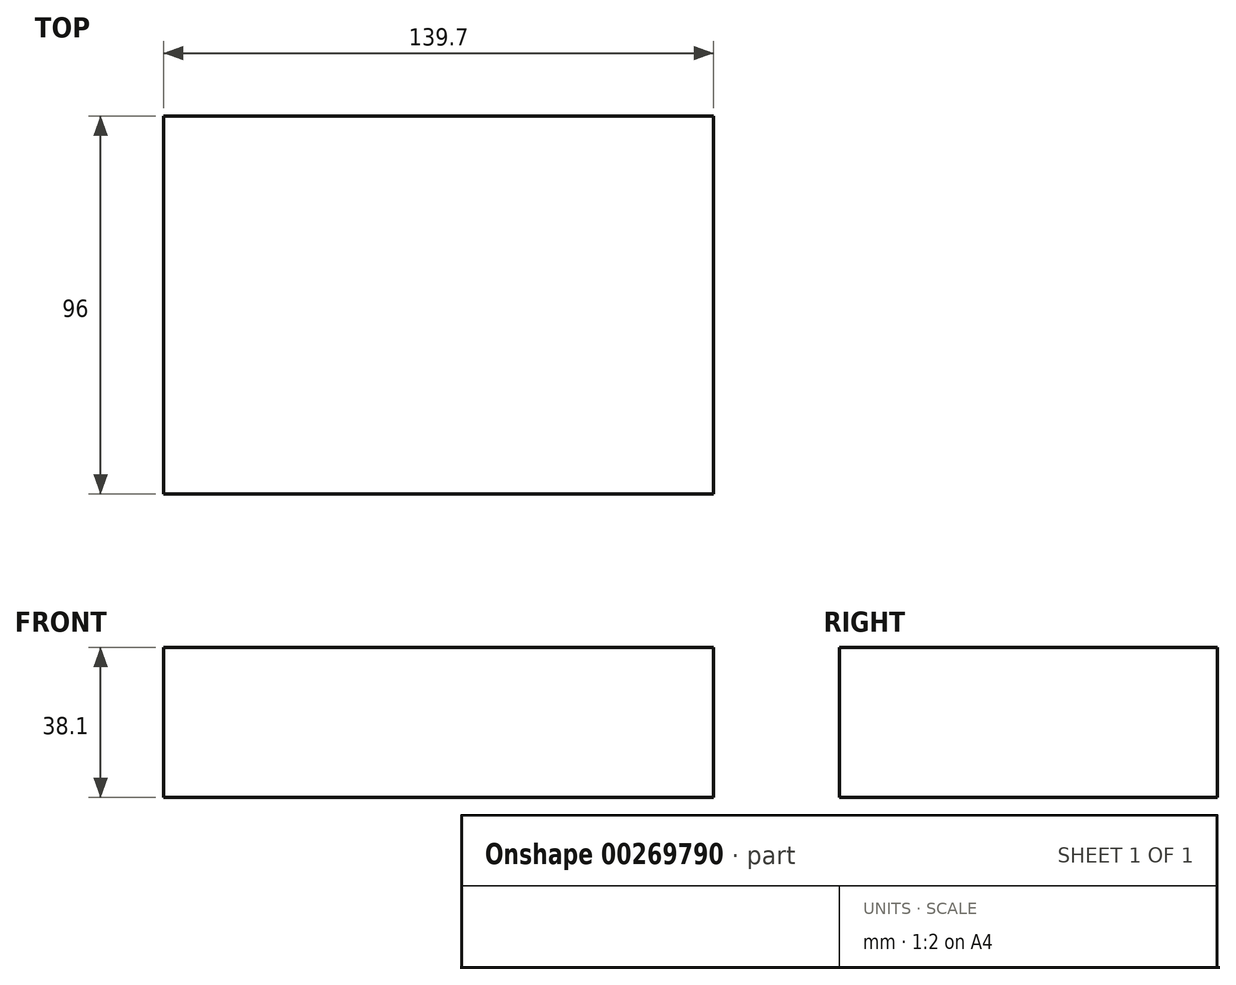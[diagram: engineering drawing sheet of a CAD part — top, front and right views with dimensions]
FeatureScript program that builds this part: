
annotation { "Feature Type Name" : "Feature", "Feature Type Description" : "" }
export const myFeature = defineFeature(function(context is Context, id is Id, definition is map)
    precondition{}
    {
        {
            var Q0;
            Q0=qCreatedBy(makeId("Front.planeOp"),FACE);
            var sketch = newSketch(context, id + "F0", { "sketchPlane" : qUnion([Q0])});
            skLineSegment(sketch, "E0", {"start": v(-361.95, 762) * mm, "end": v(361.95, 762) * mm, "construction": true});
            skPoint(sketch, "E1", {"position": v(0, 762) * mm});
            skLineSegment(sketch, "E2", {"start": v(-444.5, 457.2) * mm, "end": v(-730.25, 457.2) * mm});
            skLineSegment(sketch, "E3", {"start": v(444.5, 457.2) * mm, "end": v(730.25, 457.2) * mm});
            skLineSegment(sketch, "E4", {"start": v(-802.67, 255) * mm, "end": v(-903.42, 971.86) * mm});
            skLineSegment(sketch, "E5", {"start": v(-802.67, 255) * mm, "end": v(-361.95, 316.94) * mm, "construction": true});
            skLineSegment(sketch, "E6", {"start": v(-361.95, 762) * mm, "end": v(-361.95, 316.94) * mm, "construction": true});
            skLineSegment(sketch, "E7", {"start": v(95.25, 762) * mm, "end": v(95.25, 679.45) * mm, "construction": true});
            skLineSegment(sketch, "E8", {"start": v(-866.3, 707.76) * mm, "end": v(-784.56, 719.24) * mm, "construction": true});
            skLineSegment(sketch, "E9", {"start": v(95.25, 762) * mm, "end": v(361.95, 762) * mm, "construction": true});
            skLineSegment(sketch, "E10", {"start": v(-866.3, 707.76) * mm, "end": v(-903.42, 971.86) * mm, "construction": true});
            skLineSegment(sketch, "E11", {"start": v(-20.42, 164.2) * mm, "end": v(2.65, 0) * mm, "construction": true});
            skLineSegment(sketch, "E12", {"start": v(95.25, 679.45) * mm, "end": v(697.05, 0) * mm});
            skPoint(sketch, "E13", {"position": v(292.1, 457.2) * mm});
            skLineSegment(sketch, "E14.bottom", {"start": v(-361.95, 762) * mm, "end": v(-222.25, 762) * mm});
            skLineSegment(sketch, "E14.top", {"start": v(-361.95, 723.9) * mm, "end": v(-222.25, 723.9) * mm});
            skLineSegment(sketch, "E14.left", {"start": v(-361.95, 762) * mm, "end": v(-361.95, 723.9) * mm});
            skLineSegment(sketch, "E14.right", {"start": v(-222.25, 762) * mm, "end": v(-222.25, 723.9) * mm});
            skLineSegment(sketch, "E15.1.0.0", {"start": v(-209.55, 723.9) * mm, "end": v(-69.85, 723.9) * mm});
            skLineSegment(sketch, "E15.1.0.1", {"start": v(-69.85, 762) * mm, "end": v(-69.85, 723.9) * mm});
            skLineSegment(sketch, "E15.1.0.2", {"start": v(-209.55, 762) * mm, "end": v(-69.85, 762) * mm});
            skLineSegment(sketch, "E15.1.0.3", {"start": v(-209.55, 762) * mm, "end": v(-209.55, 723.9) * mm});
            skLineSegment(sketch, "E15.2.0.0", {"start": v(-57.15, 723.9) * mm, "end": v(82.55, 723.9) * mm});
            skLineSegment(sketch, "E15.2.0.1", {"start": v(82.55, 762) * mm, "end": v(82.55, 723.9) * mm});
            skLineSegment(sketch, "E15.2.0.2", {"start": v(-57.15, 762) * mm, "end": v(82.55, 762) * mm});
            skLineSegment(sketch, "E15.2.0.3", {"start": v(-57.15, 762) * mm, "end": v(-57.15, 723.9) * mm});
            skLineSegment(sketch, "E15.3.0.0", {"start": v(95.25, 723.9) * mm, "end": v(234.95, 723.9) * mm});
            skLineSegment(sketch, "E15.3.0.1", {"start": v(234.95, 762) * mm, "end": v(234.95, 723.9) * mm});
            skLineSegment(sketch, "E15.3.0.2", {"start": v(95.25, 762) * mm, "end": v(234.95, 762) * mm});
            skLineSegment(sketch, "E15.3.0.3", {"start": v(95.25, 762) * mm, "end": v(95.25, 723.9) * mm});
            skLineSegment(sketch, "E15.4.0.0", {"start": v(247.65, 723.9) * mm, "end": v(387.35, 723.9) * mm});
            skLineSegment(sketch, "E15.4.0.1", {"start": v(387.35, 762) * mm, "end": v(387.35, 723.9) * mm});
            skLineSegment(sketch, "E15.4.0.2", {"start": v(247.65, 762) * mm, "end": v(387.35, 762) * mm});
            skLineSegment(sketch, "E15.4.0.3", {"start": v(247.65, 762) * mm, "end": v(247.65, 723.9) * mm});
            skLineSegment(sketch, "E15.direction1", {"start": v(-361.95, 723.9) * mm, "end": v(-209.55, 723.9) * mm, "construction": true});
            skLineSegment(sketch, "E16", {"start": v(-784.56, 719.24) * mm, "end": v(-230.93, 0) * mm});
            skLineSegment(sketch, "E17", {"start": v(-451.43, 473.5) * mm, "end": v(-166.35, 453.83) * mm});
            skLineSegment(sketch, "E18", {"start": v(730.25, 457.2) * mm, "end": v(484.72, 239.73) * mm, "construction": true});
            skLineSegment(sketch, "E19", {"start": v(-166.35, 453.83) * mm, "end": v(-426.27, 253.77) * mm, "construction": true});
            skLineSegment(sketch, "E20", {"start": v(-451.43, 473.5) * mm, "end": v(-603.47, 483.98) * mm, "construction": true});
            skLineSegment(sketch, "E21", {"start": v(292.1, 457.2) * mm, "end": v(444.5, 457.2) * mm, "construction": true});
            skLineSegment(sketch, "E22", {"start": v(-426.27, 253.77) * mm, "end": v(-230.93, 0) * mm});
            skLineSegment(sketch, "E23", {"start": v(484.72, 239.73) * mm, "end": v(697.05, 0) * mm});
            skSolve(sketch);
        }
        {
            assignVariable(context, id + "F1", {"name" : "Length", "anyValue" : 96});
        }
        {
            var Q0;
            Q0=makeQuery(id+"F0.imprint","IMPRINT",FACE,{"disambiguationData":[TD([[makeQuery(id+"F0.imprint","IMPRINT",EDGE,{"derivedFrom":sQuery(id+"F0.wireOp",EDGE,"E14.bottom")}),-1.0]])]});
            extrude(context, id + "F2", {"entities" : qUnion([Q0]), "endBound" : BoundingType.SYMMETRIC, "depth" : (getVariable(context, 'Length')) * mm});
        }
    });
